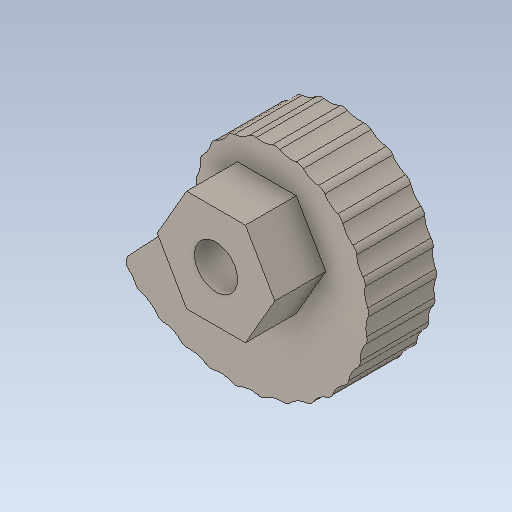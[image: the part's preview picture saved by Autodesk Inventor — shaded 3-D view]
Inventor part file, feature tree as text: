
AUTODESK INVENTOR PART (.ipt)
format: ipt  version: 2020 (Build 240168000, 168)  size: 198,144 bytes
history: native  units: in
note: dims shown in document units (in); Inventor stores cm internally (conversion verified against a paired STEP export)
features: fillet x1
ambient origin geometry x8: Origin, YZ Plane, XZ Plane, XY Plane, X Axis, Y Axis, Z Axis, Center Point
bodies: Solid1 (feature_tree)
feature tree (1):
  fillet  "Fillet1"  [1 undecoded]
note: 1 required parameter value undecoded (feature->parameter linkage not recoverable at this tier; creation-order binding heuristic only, values carry confidence <= 0.55)
